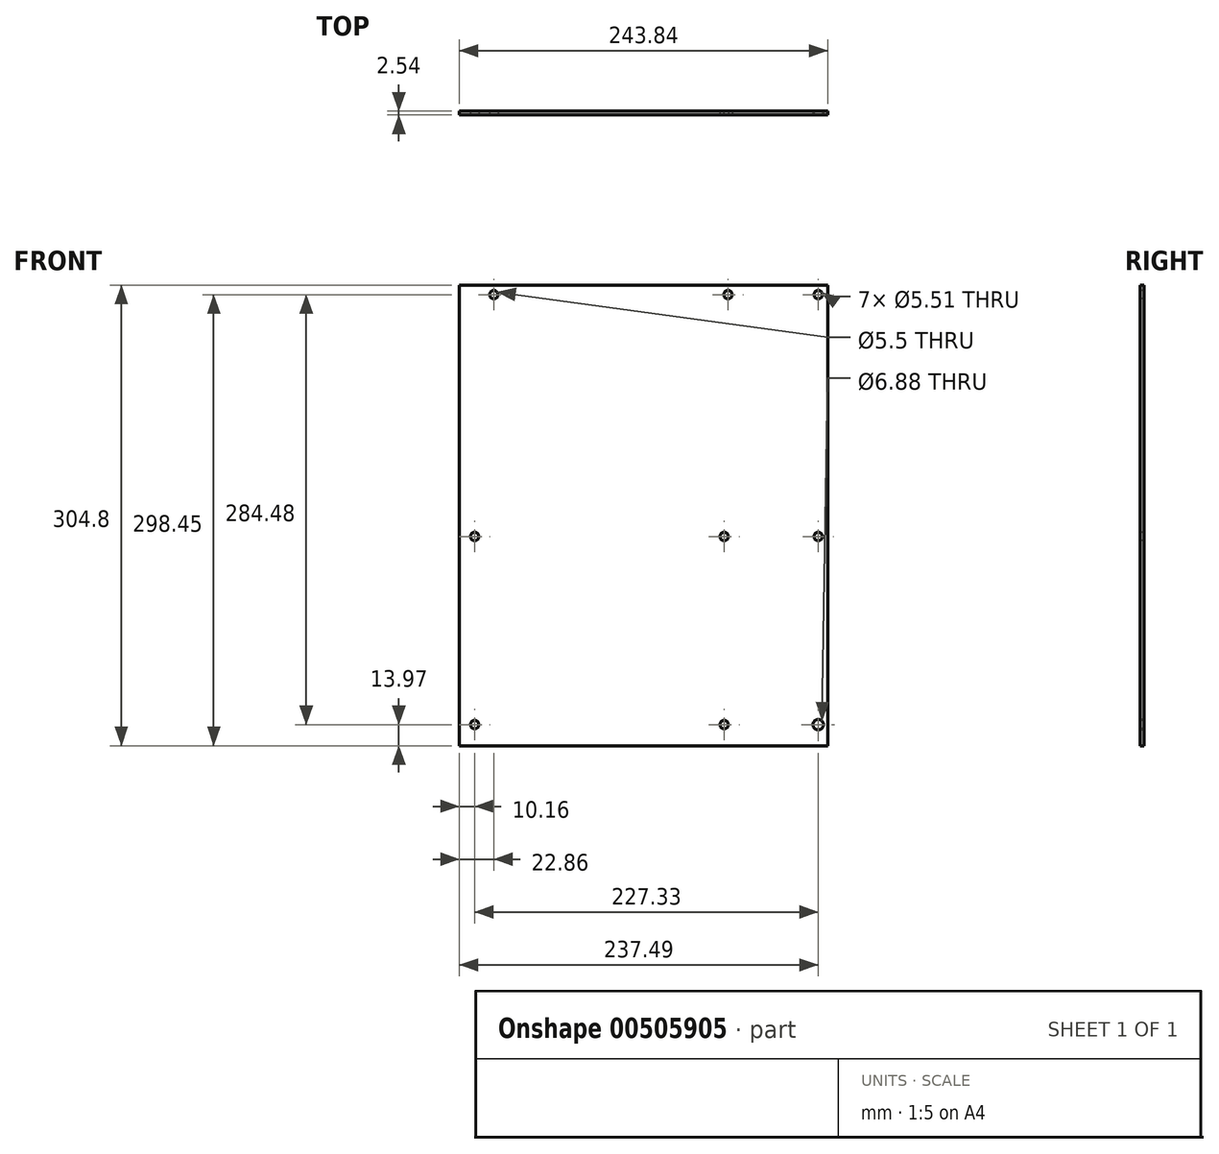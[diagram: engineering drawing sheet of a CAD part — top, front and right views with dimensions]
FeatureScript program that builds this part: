
annotation { "Feature Type Name" : "Feature", "Feature Type Description" : "" }
export const myFeature = defineFeature(function(context is Context, id is Id, definition is map)
    precondition{}
    {
        {
            var Q0;
            Q0=qCreatedBy(makeId("Front.planeOp"),FACE);
            var sketch = newSketch(context, id + "F0", { "sketchPlane" : qUnion([Q0])});
            skLineSegment(sketch, "E0", {"start": v(0, 0) * mm, "end": v(0, 304.8) * mm});
            skLineSegment(sketch, "E1", {"start": v(0, 304.8) * mm, "end": v(243.84, 304.8) * mm});
            skLineSegment(sketch, "E2", {"start": v(243.84, 304.8) * mm, "end": v(243.84, 0) * mm});
            skLineSegment(sketch, "E3", {"start": v(243.84, 0) * mm, "end": v(0, 0) * mm});
            skSolve(sketch);
        }
        {
            var Q0;
            Q0=makeQuery(id+"F0.imprint","IMPRINT",FACE,{"disambiguationData":[TD([[makeQuery(id+"F0.imprint","IMPRINT",EDGE,{"derivedFrom":sQuery(id+"F0.wireOp",EDGE,"E0")}),-1.0]])]});
            extrude(context, id + "F1", {"entities" : qUnion([Q0]), "depth" : 2.54 * mm});
        }
        {
            var Q0;
            Q0=makeQuery(id+"F1.opExtrude","CAP_FACE",FACE,{"disambiguationData":[OSD([sQuery(id+"F0.wireOp",EDGE,"E0"),sQuery(id+"F0.wireOp",EDGE,"E1"),sQuery(id+"F0.wireOp",EDGE,"E2"),sQuery(id+"F0.wireOp",EDGE,"E3")])],"isStart":false});
            var sketch = newSketch(context, id + "F2", { "sketchPlane" : qUnion([Q0])});
            skCircle(sketch, "E4", {"center": v(22.86, 298.45) * mm, "radius": 2.75 * mm});
            skCircle(sketch, "E5", {"center": v(177.8, 298.45) * mm, "radius": 2.76 * mm});
            skCircle(sketch, "E6", {"center": v(10.16, 138.43) * mm, "radius": 2.76 * mm});
            skCircle(sketch, "E7", {"center": v(237.49, 298.45) * mm, "radius": 2.76 * mm});
            skCircle(sketch, "E8", {"center": v(10.16, 13.97) * mm, "radius": 2.76 * mm});
            skCircle(sketch, "E9", {"center": v(175.26, 138.43) * mm, "radius": 2.76 * mm});
            skCircle(sketch, "E10", {"center": v(175.26, 13.97) * mm, "radius": 2.76 * mm});
            skCircle(sketch, "E11", {"center": v(237.49, 13.97) * mm, "radius": 3.44 * mm});
            skCircle(sketch, "E12", {"center": v(237.49, 138.43) * mm, "radius": 2.76 * mm});
            skSolve(sketch);
        }
        {
            var Q0;
            Q0=makeQuery(id+"F2.imprint","IMPRINT",FACE,{"disambiguationData":[TD([[makeQuery(id+"F2.imprint","IMPRINT",EDGE,{"derivedFrom":sQuery(id+"F2.wireOp",EDGE,"E4")}),1.0]])]});
            var Q1;
            Q1=makeQuery(id+"F2.imprint","IMPRINT",FACE,{"disambiguationData":[TD([[makeQuery(id+"F2.imprint","IMPRINT",EDGE,{"derivedFrom":sQuery(id+"F2.wireOp",EDGE,"E5")}),1.0]])]});
            var Q2;
            Q2=makeQuery(id+"F2.imprint","IMPRINT",FACE,{"disambiguationData":[TD([[makeQuery(id+"F2.imprint","IMPRINT",EDGE,{"derivedFrom":sQuery(id+"F2.wireOp",EDGE,"E7")}),1.0]])]});
            var Q3;
            Q3=makeQuery(id+"F2.imprint","IMPRINT",FACE,{"disambiguationData":[TD([[makeQuery(id+"F2.imprint","IMPRINT",EDGE,{"derivedFrom":sQuery(id+"F2.wireOp",EDGE,"E12")}),1.0]])]});
            var Q4;
            Q4=makeQuery(id+"F2.imprint","IMPRINT",FACE,{"disambiguationData":[TD([[makeQuery(id+"F2.imprint","IMPRINT",EDGE,{"derivedFrom":sQuery(id+"F2.wireOp",EDGE,"E9")}),1.0]])]});
            var Q5;
            Q5=makeQuery(id+"F2.imprint","IMPRINT",FACE,{"disambiguationData":[TD([[makeQuery(id+"F2.imprint","IMPRINT",EDGE,{"derivedFrom":sQuery(id+"F2.wireOp",EDGE,"E6")}),1.0]])]});
            var Q6;
            Q6=makeQuery(id+"F2.imprint","IMPRINT",FACE,{"disambiguationData":[TD([[makeQuery(id+"F2.imprint","IMPRINT",EDGE,{"derivedFrom":sQuery(id+"F2.wireOp",EDGE,"E8")}),1.0]])]});
            var Q7;
            Q7=makeQuery(id+"F2.imprint","IMPRINT",FACE,{"disambiguationData":[TD([[makeQuery(id+"F2.imprint","IMPRINT",EDGE,{"derivedFrom":sQuery(id+"F2.wireOp",EDGE,"E10")}),1.0]])]});
            var Q8;
            Q8=makeQuery(id+"F2.imprint","IMPRINT",FACE,{"disambiguationData":[TD([[makeQuery(id+"F2.imprint","IMPRINT",EDGE,{"derivedFrom":sQuery(id+"F2.wireOp",EDGE,"E11")}),1.0]])]});
            extrude(context, id + "F3", {"entities" : qUnion([Q0, Q1, Q2, Q3, Q4, Q5, Q6, Q7, Q8]), "operationType" : NewBodyOperationType.REMOVE, "oppositeDirection" : true, "depth" : 111.5 * mm});
        }
    });
